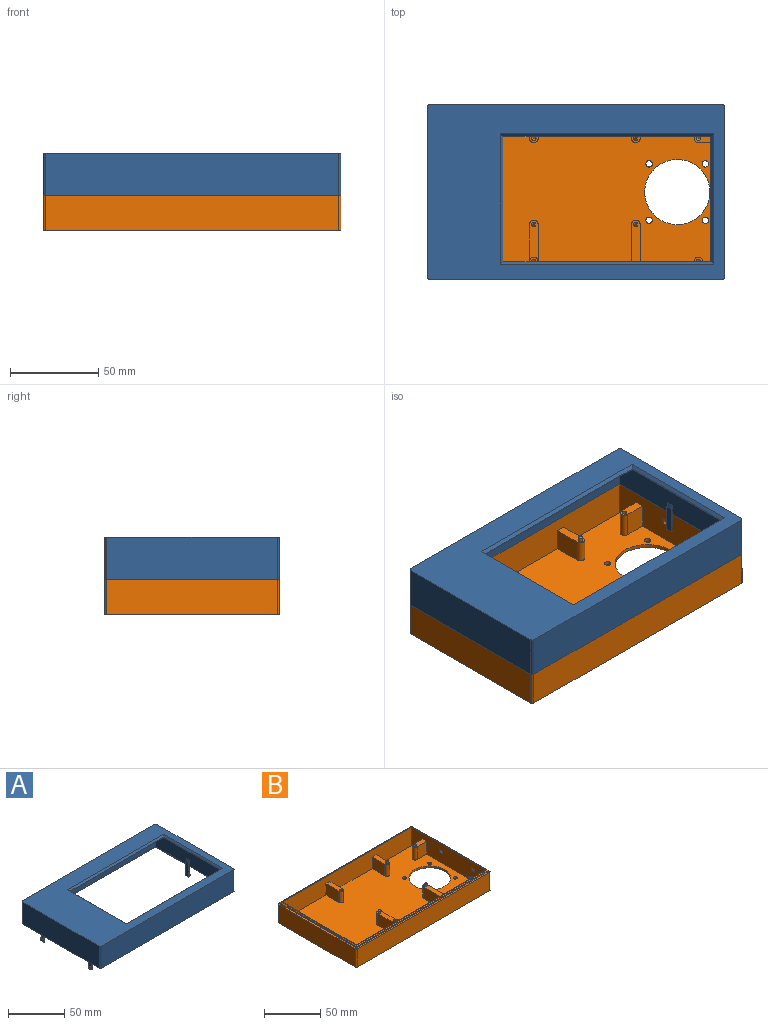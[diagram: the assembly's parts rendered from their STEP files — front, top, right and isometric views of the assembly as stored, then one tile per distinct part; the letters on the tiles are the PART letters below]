
ASSEMBLY  parts=2 mates=1
PART A: 56 faces, bbox 169x99x33.6 mm
  f0: plane 93x20mm, normal (-1,0,0), area 1815.4mm2, adj f11,f12,f13,f14,f45,f47,f48,f52
  f1: plane 93x20mm, normal (1,0,0), area 1815.4mm2, adj f11,f12,f13,f14,f30,f33,f34,f38
  f2: plane 96.6x24mm, normal (1,0,0), area 2318.4mm2, adj f10,f19,f22,f27
  f3: plane 166.6x24mm, normal (0,1,0), area 3998.4mm2, adj f10,f19,f20,f27
  f4: plane 96.6x24mm, normal (-1,0,0), area 2318.4mm2, adj f10,f20,f21,f27
  f5: plane 71x0.4mm, normal (1,0,0), area 28.4mm2, adj f6,f8,f11,f16
  f6: plane 118x0.4mm, normal (0,-1,0), area 47.2mm2, adj f5,f7,f11,f15
  f7: plane 71x0.4mm, normal (-1,0,0), area 28.4mm2, adj f6,f8,f11,f17
  f8: plane 118x0.4mm, normal (0,1,0), area 47.2mm2, adj f5,f7,f11,f18
  f9: plane 166.6x24mm, normal (0,-1,0), area 3998.4mm2, adj f10,f21,f22,f27
  f10: plane 169x99mm, normal (0,0,1), area 7736.7mm2, adj f2,f3,f4,f9,f15,f16,f17,f18
  f11: plane 163x93mm, normal (0,0,-1), area 6781mm2, adj f0,f1,f5,f6,f7,f8,f12,f13
  f12: plane 163x20mm, normal (0,-1,0), area 3260mm2, adj f0,f1,f11,f14
  f13: plane 163x20mm, normal (0,1,0), area 3260mm2, adj f0,f1,f11,f14
  f14: plane 166.2x96.2mm, normal (0,0,-1), area 829.4mm2, adj f0,f1,f12,f13,f23,f24,f25,f26
  f15: plane 121.2x1.6mm, normal (0,-0.71,0.71), area 270.6mm2, adj f6,f10,f16,f17
  f16: plane 74.2x1.6mm, normal (0.71,0,0.71), area 164.3mm2, adj f5,f10,f15,f18
  f17: plane 74.2x1.6mm, normal (-0.71,0,0.71), area 164.3mm2, adj f7,f10,f15,f18
  f18: plane 121.2x1.6mm, normal (0,0.71,0.71), area 270.6mm2, adj f8,f10,f16,f17
  f19: cylinder r=1.2mm len=24mm, axis (0,0,-1), area 45.2mm2, adj f2,f3,f10,f27
  f20: cylinder r=1.2mm len=24mm, axis (0,0,1), area 45.2mm2, adj f3,f4,f10,f27
  f21: cylinder r=1.2mm len=24mm, axis (0,0,-1), area 45.2mm2, adj f4,f9,f10,f27
  f22: cylinder r=1.2mm len=24mm, axis (0,0,1), area 45.2mm2, adj f2,f9,f10,f27
  f23: plane 96.2x2mm, normal (-1,0,0), area 192.4mm2, adj f14,f24,f26,f27
  f24: plane 166.2x2mm, normal (0,-1,0), area 332.4mm2, adj f14,f23,f25,f27
  f25: plane 96.2x2mm, normal (1,0,0), area 192.4mm2, adj f14,f24,f26,f27
  f26: plane 166.2x2mm, normal (0,1,0), area 332.4mm2, adj f14,f23,f25,f27
  f27: plane 169x99mm, normal (0,0,-1), area 741.3mm2, adj f2,f3,f4,f9,f19,f20,f21,f22
  f28: plane 3.6x0.8mm, normal (0,0,-1), area 2.9mm2, adj f29,f32,f33,f34
  f29: plane 15.62x3.6mm, normal (1,0,0), area 56.2mm2, adj f28,f30,f33,f34
  f30: plane 3.6x2.2mm, normal (0.94,0,0.34), area 8.4mm2, adj f1,f29,f33,f34
  f31: plane 8.38x3.6mm, normal (-1,0,0), area 30.2mm2, adj f14,f32,f33,f34
  f32: cylinder r=1.9mm len=3.6mm, axis (0,1,0), area 13.9mm2, adj f28,f31,f33,f34
  f33: plane 17.81x1.7mm, normal (0,-1,0), area 15.4mm2, adj f1,f28,f29,f30,f31,f32
  f34: plane 17.81x1.7mm, normal (0,1,0), area 15.4mm2, adj f1,f28,f29,f30,f31,f32
  f35: plane 8.38x3.6mm, normal (-1,0,0), area 30.2mm2, adj f14,f37,f40,f41
  f36: plane 3.6x0.8mm, normal (0,0,-1), area 2.9mm2, adj f37,f39,f40,f41
  f37: cylinder r=1.9mm len=3.6mm, axis (0,-1,0), area 13.9mm2, adj f35,f36,f40,f41
  f38: plane 3.6x2.2mm, normal (0.94,0,0.34), area 8.4mm2, adj f1,f39,f40,f41
  f39: plane 15.62x3.6mm, normal (1,0,0), area 56.2mm2, adj f36,f38,f40,f41
  f40: plane 17.81x1.7mm, normal (0,1,0), area 15.4mm2, adj f1,f35,f36,f37,f38,f39
  f41: plane 17.81x1.7mm, normal (0,-1,0), area 15.4mm2, adj f1,f35,f36,f37,f38,f39
  f42: plane 8.38x3.6mm, normal (1,0,0), area 30.2mm2, adj f14,f46,f47,f48
  f43: plane 3.6x0.8mm, normal (0,0,-1), area 2.9mm2, adj f44,f46,f47,f48
  f44: plane 15.62x3.6mm, normal (-1,0,0), area 56.2mm2, adj f43,f45,f47,f48
  f45: plane 3.6x2.2mm, normal (-0.94,0,0.34), area 8.4mm2, adj f0,f44,f47,f48
  f46: cylinder r=1.9mm len=3.6mm, axis (0,-1,0), area 13.9mm2, adj f42,f43,f47,f48
  f47: plane 17.81x1.7mm, normal (0,1,0), area 15.4mm2, adj f0,f42,f43,f44,f45,f46
  f48: plane 17.81x1.7mm, normal (0,-1,0), area 15.4mm2, adj f0,f42,f43,f44,f45,f46
  f49: plane 3.6x0.8mm, normal (0,0,-1), area 2.9mm2, adj f50,f53,f54,f55
  f50: cylinder r=1.9mm len=3.6mm, axis (0,1,0), area 13.9mm2, adj f49,f51,f54,f55
  f51: plane 8.38x3.6mm, normal (1,0,0), area 30.2mm2, adj f14,f50,f54,f55
  f52: plane 3.6x2.2mm, normal (-0.94,0,0.34), area 8.4mm2, adj f0,f53,f54,f55
  f53: plane 15.62x3.6mm, normal (-1,0,0), area 56.2mm2, adj f49,f52,f54,f55
  f54: plane 17.81x1.7mm, normal (0,-1,0), area 15.4mm2, adj f0,f49,f50,f51,f52,f53
  f55: plane 17.81x1.7mm, normal (0,1,0), area 15.4mm2, adj f0,f49,f50,f51,f52,f53
PART B: 84 faces, bbox 169x99x22 mm
  f0: plane 166.6x20mm, normal (0,1,0), area 3332mm2, adj f7,f71,f74,f79
  f1: plane 96.6x20mm, normal (-1,0,0), area 1932mm2, adj f7,f71,f72,f79
  f2: plane 166.6x20mm, normal (0,-1,0), area 3332mm2, adj f7,f72,f73,f79
  f3: plane 96.6x20mm, normal (1,0,0), area 1932mm2, adj f7,f73,f74,f79
  f4: plane 93x20mm, normal (1,0,0), area 1832.3mm2, adj f6,f8,f9,f10,f54,f55,f56,f60
  f5: plane 93x20mm, normal (-1,0,0), area 1762.3mm2, adj f6,f8,f9,f10,f19,f21,f22,f57
  f6: plane 163x93mm, normal (0,0,1), area 13449.2mm2, adj f4,f5,f8,f9,f11,f12,f13,f16
  f7: plane 169x99mm, normal (0,0,-1), area 15613.8mm2, adj f0,f1,f2,f3,f66,f67,f68,f69
  f8: plane 163x20mm, normal (0,1,0), area 3057.5mm2, adj f4,f5,f6,f10,f12,f13,f14,f16
  f9: plane 163x20mm, normal (0,-1,0), area 3135mm2, adj f4,f5,f6,f10,f23,f25,f26,f27
  f10: plane 164.2x94.2mm, normal (0,0,1), area 308.6mm2, adj f4,f5,f8,f9,f80,f81,f82,f83
  f11: cylinder r=2.5mm len=14mm, axis (0,0,-1), area 110mm2, adj f6,f12,f13,f14
  f12: plane 14x7mm, normal (-1,0,0), area 98mm2, adj f6,f8,f11,f14
  f13: plane 14x7mm, normal (1,0,0), area 98mm2, adj f6,f8,f11,f14
  f14: plane 9.5x5mm, normal (0,0,1), area 39.5mm2, adj f8,f11,f12,f13,f42
  f15: cylinder r=2.5mm len=5mm, axis (0,0,-1), area 11.8mm2, adj f16,f17,f18,f32
  f16: plane 28x14mm, normal (-1,0,0), area 360.5mm2, adj f6,f8,f15,f18,f31,f32
  f17: plane 28x14mm, normal (1,0,0), area 360.5mm2, adj f6,f8,f15,f18,f31,f32
  f18: plane 9.5x5mm, normal (0,0,1), area 39.5mm2, adj f8,f15,f16,f17,f40
  f19: plane 14x12mm, normal (0,1,0), area 168mm2, adj f5,f6,f20,f22
  f20: cylinder r=2.5mm len=14mm, axis (0,0,-1), area 110mm2, adj f6,f19,f21,f22
  f21: plane 14x12mm, normal (0,-1,0), area 168mm2, adj f5,f6,f20,f22
  f22: plane 14.5x5mm, normal (0,0,1), area 64.5mm2, adj f5,f19,f20,f21,f38
  f23: plane 16x12.5mm, normal (-1,0,0), area 200mm2, adj f6,f9,f24,f26
  f24: cylinder r=2.5mm len=12.5mm, axis (0,0,-1), area 98.2mm2, adj f6,f23,f25,f26
  f25: plane 16x12.5mm, normal (1,0,0), area 200mm2, adj f6,f9,f24,f26
  f26: plane 18.5x5mm, normal (0,0,1), area 84.5mm2, adj f9,f23,f24,f25,f44
  f27: plane 16x12.5mm, normal (-1,0,0), area 200mm2, adj f6,f9,f28,f30
  f28: cylinder r=2.5mm len=12.5mm, axis (0,0,-1), area 98.2mm2, adj f6,f27,f29,f30
  f29: plane 16x12.5mm, normal (1,0,0), area 200mm2, adj f6,f9,f28,f30
  f30: plane 18.5x5mm, normal (0,0,1), area 85.3mm2, adj f9,f27,f28,f29,f49
  f31: cylinder r=2.5mm len=12.5mm, axis (0,0,-1), area 98.2mm2, adj f6,f16,f17,f32
  f32: plane 23.5x5mm, normal (0,0,1), area 100.5mm2, adj f15,f16,f17,f31,f45
  f33: cylinder r=2.5mm len=12.5mm, axis (0,0,-1), area 98.2mm2, adj f6,f34,f35,f36
  f34: plane 28x12.5mm, normal (-1,0,0), area 350mm2, adj f6,f8,f33,f36
  f35: plane 28x12.5mm, normal (1,0,0), area 350mm2, adj f6,f8,f33,f36
  f36: plane 30.5x5mm, normal (0,0,1), area 145.3mm2, adj f8,f33,f34,f35,f47
  f37: cone r=0mm half-angle=59deg, axis (0,0,1), area 6.2mm2, adj f38
  f38: cylinder r=1.3mm len=4mm, axis (0,0,1), area 32.7mm2, adj f22,f37
  f39: cone r=0mm half-angle=59deg, axis (0,0,1), area 6.2mm2, adj f40
  f40: cylinder r=1.3mm len=4mm, axis (0,0,1), area 32.7mm2, adj f18,f39
  f41: cone r=0mm half-angle=59deg, axis (0,0,1), area 6.2mm2, adj f42
  f42: cylinder r=1.3mm len=4mm, axis (0,0,1), area 32.7mm2, adj f14,f41
  f43: cone r=0mm half-angle=59deg, axis (0,0,1), area 6.2mm2, adj f44
  f44: cylinder r=1.3mm len=4mm, axis (0,0,1), area 32.7mm2, adj f26,f43
  f45: cylinder r=1.2mm len=2.4mm, axis (0,0,-1), area 16.6mm2, adj f32,f53
  f46: plane 0.8x0.8mm, normal (0,0,1), area 0.5mm2, adj f53
  f47: cylinder r=1.2mm len=2.4mm, axis (0,0,-1), area 16.6mm2, adj f36,f51
  f48: plane 0.8x0.8mm, normal (0,0,1), area 0.5mm2, adj f51
  f49: cylinder r=1.2mm len=2.4mm, axis (0,0,-1), area 16.6mm2, adj f30,f52
  f50: plane 0.8x0.8mm, normal (0,0,1), area 0.5mm2, adj f52
  f51: cone r=0.4mm half-angle=45deg, axis (0,0,-1), area 5.7mm2, adj f47,f48
  f52: cone r=0.4mm half-angle=45deg, axis (0,0,-1), area 5.7mm2, adj f49,f50
  f53: cone r=0.4mm half-angle=45deg, axis (0,0,-1), area 5.7mm2, adj f45,f46
  f54: cylinder r=2mm len=4mm, axis (0,1,0), area 16.8mm2, adj f4,f55,f56
  f55: plane 3.46x1mm, normal (0,1,0), area 2.5mm2, adj f4,f54
  f56: plane 3.46x1mm, normal (0,-1,0), area 2.5mm2, adj f4,f54
  f57: cylinder r=2mm len=4mm, axis (0,1,0), area 16.8mm2, adj f5,f58,f59
  f58: plane 3.46x1mm, normal (0,1,0), area 2.5mm2, adj f5,f57
  f59: plane 3.46x1mm, normal (0,-1,0), area 2.5mm2, adj f5,f57
  f60: cylinder r=2mm len=4mm, axis (0,-1,0), area 16.8mm2, adj f4,f61,f62
  f61: plane 3.46x1mm, normal (0,-1,0), area 2.5mm2, adj f4,f60
  f62: plane 3.46x1mm, normal (0,1,0), area 2.5mm2, adj f4,f60
  f63: cylinder r=2mm len=4mm, axis (0,-1,0), area 16.8mm2, adj f5,f64,f65
  f64: plane 3.46x1mm, normal (0,-1,0), area 2.5mm2, adj f5,f63
  f65: plane 3.46x1mm, normal (0,1,0), area 2.5mm2, adj f5,f63
  f66: cylinder r=18.5mm len=37mm, axis (0,0,1), area 232.5mm2, adj f6,f7
  f67: cylinder r=1.8mm len=3.6mm, axis (0,0,1), area 22.6mm2, adj f6,f7
  f68: cylinder r=1.8mm len=3.6mm, axis (0,0,1), area 22.6mm2, adj f6,f7
  f69: cylinder r=1.8mm len=3.6mm, axis (0,0,1), area 22.6mm2, adj f6,f7
  f70: cylinder r=1.8mm len=3.6mm, axis (0,0,1), area 22.6mm2, adj f6,f7
  f71: cylinder r=1.2mm len=20mm, axis (0,0,1), area 37.7mm2, adj f0,f1,f7,f79
  f72: cylinder r=1.2mm len=20mm, axis (0,0,-1), area 37.7mm2, adj f1,f2,f7,f79
  f73: cylinder r=1.2mm len=20mm, axis (0,0,1), area 37.7mm2, adj f2,f3,f7,f79
  f74: cylinder r=1.2mm len=20mm, axis (0,0,-1), area 37.7mm2, adj f0,f3,f7,f79
  f75: plane 165.8x1.2mm, normal (0,1,0), area 199mm2, adj f76,f78,f79,f83
  f76: plane 95.8x1.2mm, normal (1,0,0), area 115mm2, adj f75,f77,f79,f82
  f77: plane 165.8x1.2mm, normal (0,-1,0), area 199mm2, adj f76,f78,f79,f80
  f78: plane 95.8x1.2mm, normal (-1,0,0), area 115mm2, adj f75,f77,f79,f81
  f79: plane 169x99mm, normal (0,0,1), area 846.1mm2, adj f0,f1,f2,f3,f71,f72,f73,f74
  f80: plane 165.8x0.8mm, normal (0,-0.71,0.71), area 186.7mm2, adj f10,f77,f81,f82
  f81: plane 95.8x0.8mm, normal (-0.71,0,0.71), area 107.5mm2, adj f10,f78,f80,f83
  f82: plane 95.8x0.8mm, normal (0.71,0,0.71), area 107.5mm2, adj f10,f76,f80,f83
  f83: plane 165.8x0.8mm, normal (0,0.71,0.71), area 186.7mm2, adj f10,f75,f81,f82
PLACE A t=(50.33,56.71,77.43)mm
PLACE B t=(32.83,60.71,35.43)mm
MATE planar B.f79 <-> A.f27  axis (0,0,1) through (32.83,60.71,55.43)mm
